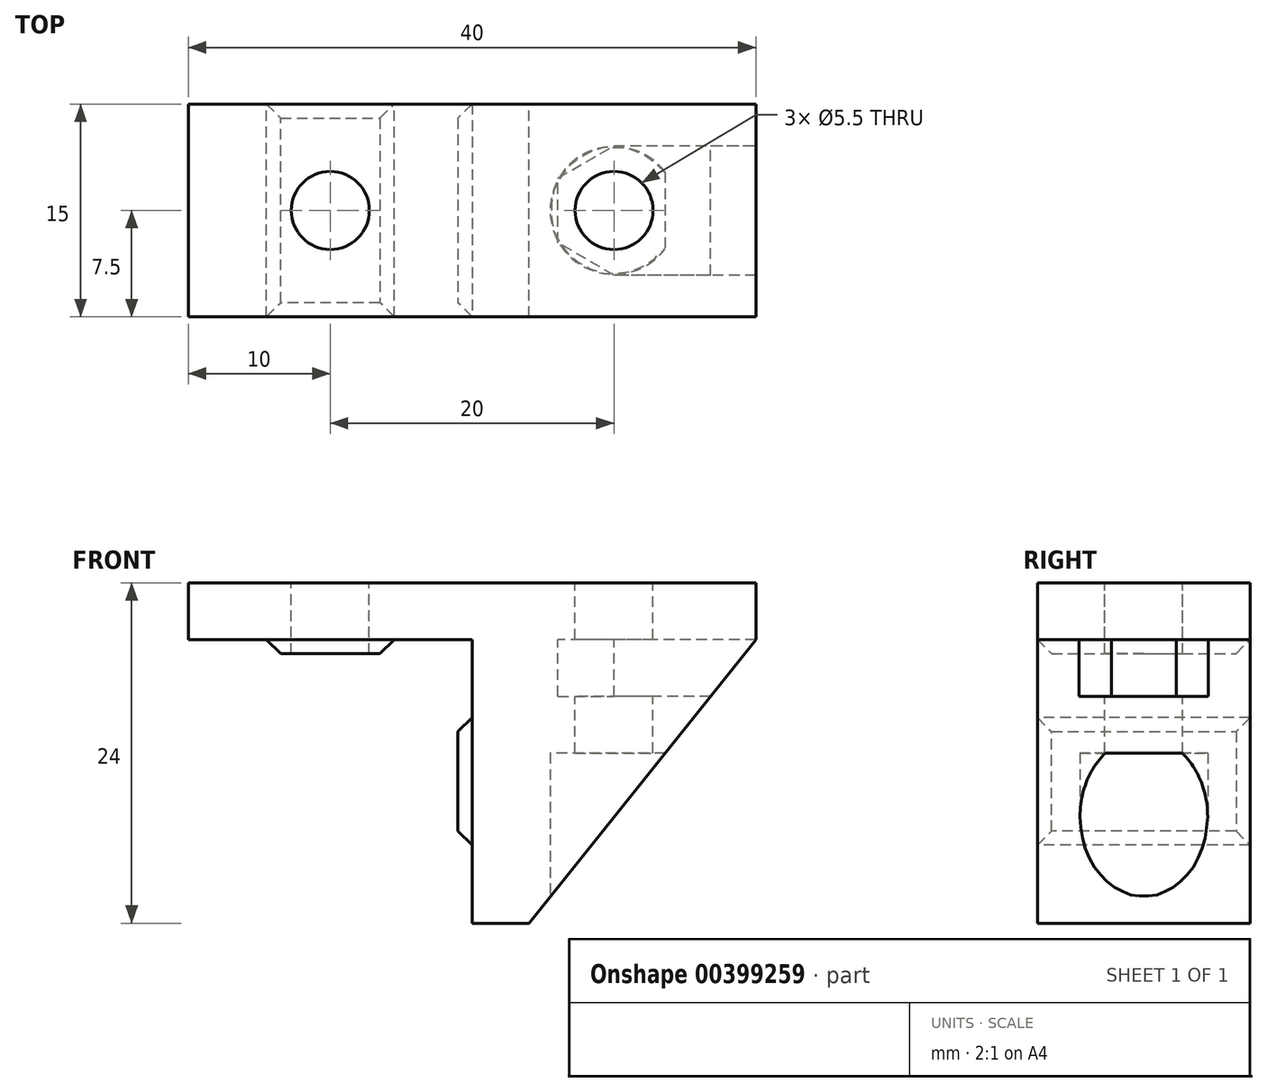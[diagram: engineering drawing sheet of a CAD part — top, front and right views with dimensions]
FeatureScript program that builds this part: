
annotation { "Feature Type Name" : "Feature", "Feature Type Description" : "" }
export const myFeature = defineFeature(function(context is Context, id is Id, definition is map)
    precondition{}
    {
        {
            var Q0;
            Q0=qCreatedBy(makeId("Top.planeOp"),FACE);
            var sketch = newSketch(context, id + "F0", { "sketchPlane" : qUnion([Q0])});
            skLineSegment(sketch, "E0.bottom", {"start": v(0, 0) * mm, "end": v(40, 0) * mm});
            skLineSegment(sketch, "E0.top", {"start": v(0, 15) * mm, "end": v(40, 15) * mm});
            skLineSegment(sketch, "E0.left", {"start": v(0, 0) * mm, "end": v(0, 15) * mm});
            skLineSegment(sketch, "E0.right", {"start": v(40, 0) * mm, "end": v(40, 15) * mm});
            skSolve(sketch);
        }
        {
            var Q0;
            Q0=makeQuery(id+"F0.imprint","IMPRINT",FACE,{"disambiguationData":[TD([[makeQuery(id+"F0.imprint","IMPRINT",EDGE,{"derivedFrom":sQuery(id+"F0.wireOp",EDGE,"E0.bottom")}),1.0]])]});
            extrude(context, id + "F1", {"entities" : qUnion([Q0]), "depth" : 4 * mm});
        }
        {
            var Q0;
            Q0=makeQuery(id+"F1.opExtrude","CAP_FACE",FACE,{"disambiguationData":[OSD([sQuery(id+"F0.wireOp",EDGE,"E0.bottom"),sQuery(id+"F0.wireOp",EDGE,"E0.top"),sQuery(id+"F0.wireOp",EDGE,"E0.left"),sQuery(id+"F0.wireOp",EDGE,"E0.right")])],"isStart":true});
            var sketch = newSketch(context, id + "F2", { "sketchPlane" : qUnion([Q0])});
            skLineSegment(sketch, "E1.bottom", {"start": v(5.5, 0) * mm, "end": v(14.5, 0) * mm});
            skLineSegment(sketch, "E1.top", {"start": v(5.5, -15) * mm, "end": v(14.5, -15) * mm});
            skLineSegment(sketch, "E1.left", {"start": v(5.5, 0) * mm, "end": v(5.5, -15) * mm});
            skLineSegment(sketch, "E1.right", {"start": v(14.5, 0) * mm, "end": v(14.5, -15) * mm});
            skLineSegment(sketch, "E2.bottom", {"start": v(20, 0) * mm, "end": v(24, 0) * mm});
            skLineSegment(sketch, "E2.top", {"start": v(20, -15) * mm, "end": v(24, -15) * mm});
            skLineSegment(sketch, "E2.left", {"start": v(20, 0) * mm, "end": v(20, -15) * mm});
            skLineSegment(sketch, "E2.right", {"start": v(24, 0) * mm, "end": v(24, -15) * mm});
            skSolve(sketch);
        }
        {
            var Q0;
            Q0 = qSketchRegion(id + "F2", true);
            extrude(context, id + "F3", {"entities" : qUnion([Q0]), "operationType" : NewBodyOperationType.ADD, "depth" : 1 * mm});
        }
        {
            var Q0;
            Q0=makeQuery(id+"F3.opExtrude","CAP_FACE",FACE,{"disambiguationData":[OSD([sQuery(id+"F2.wireOp",EDGE,"E2.bottom"),sQuery(id+"F2.wireOp",EDGE,"E2.top"),sQuery(id+"F2.wireOp",EDGE,"E2.left"),sQuery(id+"F2.wireOp",EDGE,"E2.right")])],"isStart":false});
            extrude(context, id + "F4", {"entities" : qUnion([Q0]), "operationType" : NewBodyOperationType.ADD, "depth" : 19 * mm});
        }
        {
            var Q0;
            {var subQ0=sQuery(id+"F2.wireOp",EDGE,"E2.left");Q0=makeQuery(id+"F4.boolean.opBoolean","MERGE",FACE,{"derivedFrom":[makeQuery(id+"F3.opExtrude","SWEPT_FACE",FACE,{"disambiguationData":[OSD([subQ0])]}),makeQuery(id+"F4.opExtrude","SWEPT_FACE",FACE,{"disambiguationData":[OSD([subQ0])]})]});}
            var sketch = newSketch(context, id + "F5", { "sketchPlane" : qUnion([Q0])});
            skLineSegment(sketch, "E3.bottom", {"start": v(-15, -14.5) * mm, "end": v(0, -14.5) * mm});
            skLineSegment(sketch, "E3.top", {"start": v(-15, -5.5) * mm, "end": v(0, -5.5) * mm});
            skLineSegment(sketch, "E3.left", {"start": v(-15, -14.5) * mm, "end": v(-15, -5.5) * mm});
            skLineSegment(sketch, "E3.right", {"start": v(0, -14.5) * mm, "end": v(0, -5.5) * mm});
            skSolve(sketch);
        }
        {
            var Q0;
            Q0=makeQuery(id+"F5.imprint","IMPRINT",FACE,{"disambiguationData":[TD([[makeQuery(id+"F5.imprint","IMPRINT",EDGE,{"derivedFrom":sQuery(id+"F5.wireOp",EDGE,"E3.bottom")}),1.0]])]});
            extrude(context, id + "F6", {"entities" : qUnion([Q0]), "operationType" : NewBodyOperationType.ADD, "depth" : 1 * mm});
        }
        {
            var Q0;
            Q0=makeQuery(id+"F6.opExtrude","CAP_FACE",FACE,{"disambiguationData":[OSD([sQuery(id+"F5.wireOp",EDGE,"E3.bottom"),sQuery(id+"F5.wireOp",EDGE,"E3.top"),sQuery(id+"F5.wireOp",EDGE,"E3.left"),sQuery(id+"F5.wireOp",EDGE,"E3.right")])],"isStart":false});
            var Q1;
            Q1=makeQuery(id+"F3.opExtrude","CAP_FACE",FACE,{"disambiguationData":[OSD([sQuery(id+"F2.wireOp",EDGE,"E1.bottom"),sQuery(id+"F2.wireOp",EDGE,"E1.top"),sQuery(id+"F2.wireOp",EDGE,"E1.left"),sQuery(id+"F2.wireOp",EDGE,"E1.right")])],"isStart":false});
            chamfer(context, id + "F7", {"entities" : qUnion([Q0, Q1]), "width" : 1 * mm, "tangentPropagation" : true});
        }
        {
            var Q0;
            {var subQ0=sQuery(id+"F2.wireOp",EDGE,"E2.bottom");Q0=makeQuery(id+"F6.boolean.opBoolean","MERGE",FACE,{"derivedFrom":[makeQuery(id+"F4.boolean.opBoolean","MERGE",FACE,{"derivedFrom":[makeQuery(id+"F3.boolean.opBoolean","MERGE",FACE,{"derivedFrom":[makeQuery(id+"F1.opExtrude","SWEPT_FACE",FACE,{"disambiguationData":[OSD([sQuery(id+"F0.wireOp",EDGE,"E0.bottom")])]}),makeQuery(id+"F3.opExtrude","SWEPT_FACE",FACE,{"disambiguationData":[OSD([sQuery(id+"F2.wireOp",EDGE,"E1.bottom")])]}),makeQuery(id+"F3.opExtrude","SWEPT_FACE",FACE,{"disambiguationData":[OSD([subQ0])]})]}),makeQuery(id+"F4.opExtrude","SWEPT_FACE",FACE,{"disambiguationData":[OSD([subQ0])]})]}),makeQuery(id+"F6.opExtrude","SWEPT_FACE",FACE,{"disambiguationData":[OSD([sQuery(id+"F5.wireOp",EDGE,"E3.right")])]})]});}
            var sketch = newSketch(context, id + "F8", { "sketchPlane" : qUnion([Q0])});
            skLineSegment(sketch, "E4.0", {"start": v(24, 0) * mm, "end": v(40, 0) * mm});
            skLineSegment(sketch, "E5.0", {"start": v(24, -20) * mm, "end": v(24, 0) * mm});
            skLineSegment(sketch, "E6", {"start": v(40, 0) * mm, "end": v(24, -20) * mm});
            skSolve(sketch);
        }
        {
            var Q0;
            Q0=makeQuery(id+"F8.imprint","IMPRINT",FACE,{"disambiguationData":[TD([[makeQuery(id+"F8.imprint","IMPRINT",EDGE,{"derivedFrom":sQuery(id+"F8.wireOp",EDGE,"E4.0")}),-1.0]])]});
            var Q1;
            {var subQ0=sQuery(id+"F2.wireOp",EDGE,"E2.top");Q1=makeQuery(id+"F6.boolean.opBoolean","MERGE",FACE,{"derivedFrom":[makeQuery(id+"F4.boolean.opBoolean","MERGE",FACE,{"derivedFrom":[makeQuery(id+"F3.boolean.opBoolean","MERGE",FACE,{"derivedFrom":[makeQuery(id+"F1.opExtrude","SWEPT_FACE",FACE,{"disambiguationData":[OSD([sQuery(id+"F0.wireOp",EDGE,"E0.top")])]}),makeQuery(id+"F3.opExtrude","SWEPT_FACE",FACE,{"disambiguationData":[OSD([sQuery(id+"F2.wireOp",EDGE,"E1.top")])]}),makeQuery(id+"F3.opExtrude","SWEPT_FACE",FACE,{"disambiguationData":[OSD([subQ0])]})]}),makeQuery(id+"F4.opExtrude","SWEPT_FACE",FACE,{"disambiguationData":[OSD([subQ0])]})]}),makeQuery(id+"F6.opExtrude","SWEPT_FACE",FACE,{"disambiguationData":[OSD([sQuery(id+"F5.wireOp",EDGE,"E3.left")])]})]});}
            extrude(context, id + "F9", {"entities" : qUnion([Q0]), "operationType" : NewBodyOperationType.ADD, "endBound" : BoundingType.UP_TO_SURFACE, "oppositeDirection" : true, "endBoundEntityFace" : qUnion([Q1]), "depth" : 25 * mm});
        }
        {
            var Q0;
            Q0=makeQuery(id+"F1.opExtrude","CAP_FACE",FACE,{"disambiguationData":[OSD([sQuery(id+"F0.wireOp",EDGE,"E0.bottom"),sQuery(id+"F0.wireOp",EDGE,"E0.top"),sQuery(id+"F0.wireOp",EDGE,"E0.left"),sQuery(id+"F0.wireOp",EDGE,"E0.right")])],"isStart":false});
            cPlane(context, id + "F10", {"entities" : qUnion([Q0]), "cplaneType" : CPlaneType.OFFSET, "offset" : 4 * mm, "oppositeDirection" : true, "width" : 150 * mm, "height" : 150 * mm});
        }
        {
            var Q0;
            Q0=qCreatedBy(id+"F10.planeOp",FACE);
            var sketch = newSketch(context, id + "F11", { "sketchPlane" : qUnion([Q0])});
            skLineSegment(sketch, "E7.0.0", {"start": v(40, 15) * mm, "end": v(0, 15) * mm, "construction": true});
            skLineSegment(sketch, "E7.0.1", {"start": v(0, 15) * mm, "end": v(0, 0) * mm, "construction": true});
            skLineSegment(sketch, "E7.0.2", {"start": v(0, 0) * mm, "end": v(40, 0) * mm, "construction": true});
            skLineSegment(sketch, "E7.0.3", {"start": v(40, 0) * mm, "end": v(40, 15) * mm, "construction": true});
            skCircle(sketch, "E8.cCircle", {"center": v(30, 7.5) * mm, "radius": 3.95 * mm, "construction": true});
            skPoint(sketch, "E8.cCircle.centerSnap0", {"position": v(40, 7.5) * mm});
            skLineSegment(sketch, "E8.0", {"start": v(33.95, 9.78) * mm, "end": v(33.95, 5.22) * mm, "construction": true});
            skLineSegment(sketch, "E8.1", {"start": v(33.95, 5.22) * mm, "end": v(30, 2.94) * mm, "construction": true});
            skLineSegment(sketch, "E8.2", {"start": v(30, 2.94) * mm, "end": v(26.05, 5.22) * mm});
            skLineSegment(sketch, "E8.3", {"start": v(26.05, 5.22) * mm, "end": v(26.05, 9.78) * mm});
            skLineSegment(sketch, "E8.4", {"start": v(26.05, 9.78) * mm, "end": v(30, 12.06) * mm});
            skLineSegment(sketch, "E8.5", {"start": v(30, 12.06) * mm, "end": v(33.95, 9.78) * mm, "construction": true});
            skPoint(sketch, "E8.0.midPoint", {"position": v(33.95, 7.5) * mm});
            skLineSegment(sketch, "E9", {"start": v(30, 12.06) * mm, "end": v(40, 12.06) * mm});
            skLineSegment(sketch, "E10", {"start": v(40, 12.06) * mm, "end": v(40, 2.94) * mm});
            skLineSegment(sketch, "E11", {"start": v(40, 2.94) * mm, "end": v(30, 2.94) * mm});
            skSolve(sketch);
        }
        {
            var Q0;
            Q0 = qSketchRegion(id + "F11", true);
            extrude(context, id + "F12", {"entities" : qUnion([Q0]), "operationType" : NewBodyOperationType.REMOVE, "oppositeDirection" : true, "depth" : 4 * mm});
        }
        {
            var Q0;
            Q0=makeQuery(id+"F1.opExtrude","CAP_FACE",FACE,{"disambiguationData":[OSD([sQuery(id+"F0.wireOp",EDGE,"E0.bottom"),sQuery(id+"F0.wireOp",EDGE,"E0.top"),sQuery(id+"F0.wireOp",EDGE,"E0.left"),sQuery(id+"F0.wireOp",EDGE,"E0.right")])],"isStart":false});
            var sketch = newSketch(context, id + "F13", { "sketchPlane" : qUnion([Q0])});
            skCircle(sketch, "E12", {"center": v(30, 7.5) * mm, "radius": 2.75 * mm});
            skPoint(sketch, "E12.centerSnap0", {"position": v(40, 7.5) * mm});
            skCircle(sketch, "E13", {"center": v(10, 7.5) * mm, "radius": 2.75 * mm});
            skSolve(sketch);
        }
        {
            var Q0;
            Q0 = qSketchRegion(id + "F13", true);
            extrude(context, id + "F14", {"entities" : qUnion([Q0]), "operationType" : NewBodyOperationType.REMOVE, "endBound" : BoundingType.THROUGH_ALL, "oppositeDirection" : true, "depth" : 25 * mm});
        }
        {
            var Q0;
            Q0=makeQuery(id+"F4.opExtrude","CAP_FACE",FACE,{"disambiguationData":[OSD([sQuery(id+"F2.wireOp",EDGE,"E2.bottom"),sQuery(id+"F2.wireOp",EDGE,"E2.top"),sQuery(id+"F2.wireOp",EDGE,"E2.left"),sQuery(id+"F2.wireOp",EDGE,"E2.right")])],"isStart":false});
            var sketch = newSketch(context, id + "F15", { "sketchPlane" : qUnion([Q0])});
            skCircle(sketch, "E14.0", {"center": v(30, -7.5) * mm, "radius": 2.75 * mm, "construction": true});
            skCircle(sketch, "E15", {"center": v(30, -7.5) * mm, "radius": 4.5 * mm});
            skSolve(sketch);
        }
        {
            var Q0;
            Q0 = qSketchRegion(id + "F15", true);
            extrude(context, id + "F16", {"entities" : qUnion([Q0]), "operationType" : NewBodyOperationType.REMOVE, "oppositeDirection" : true, "depth" : 12 * mm});
        }
    });
